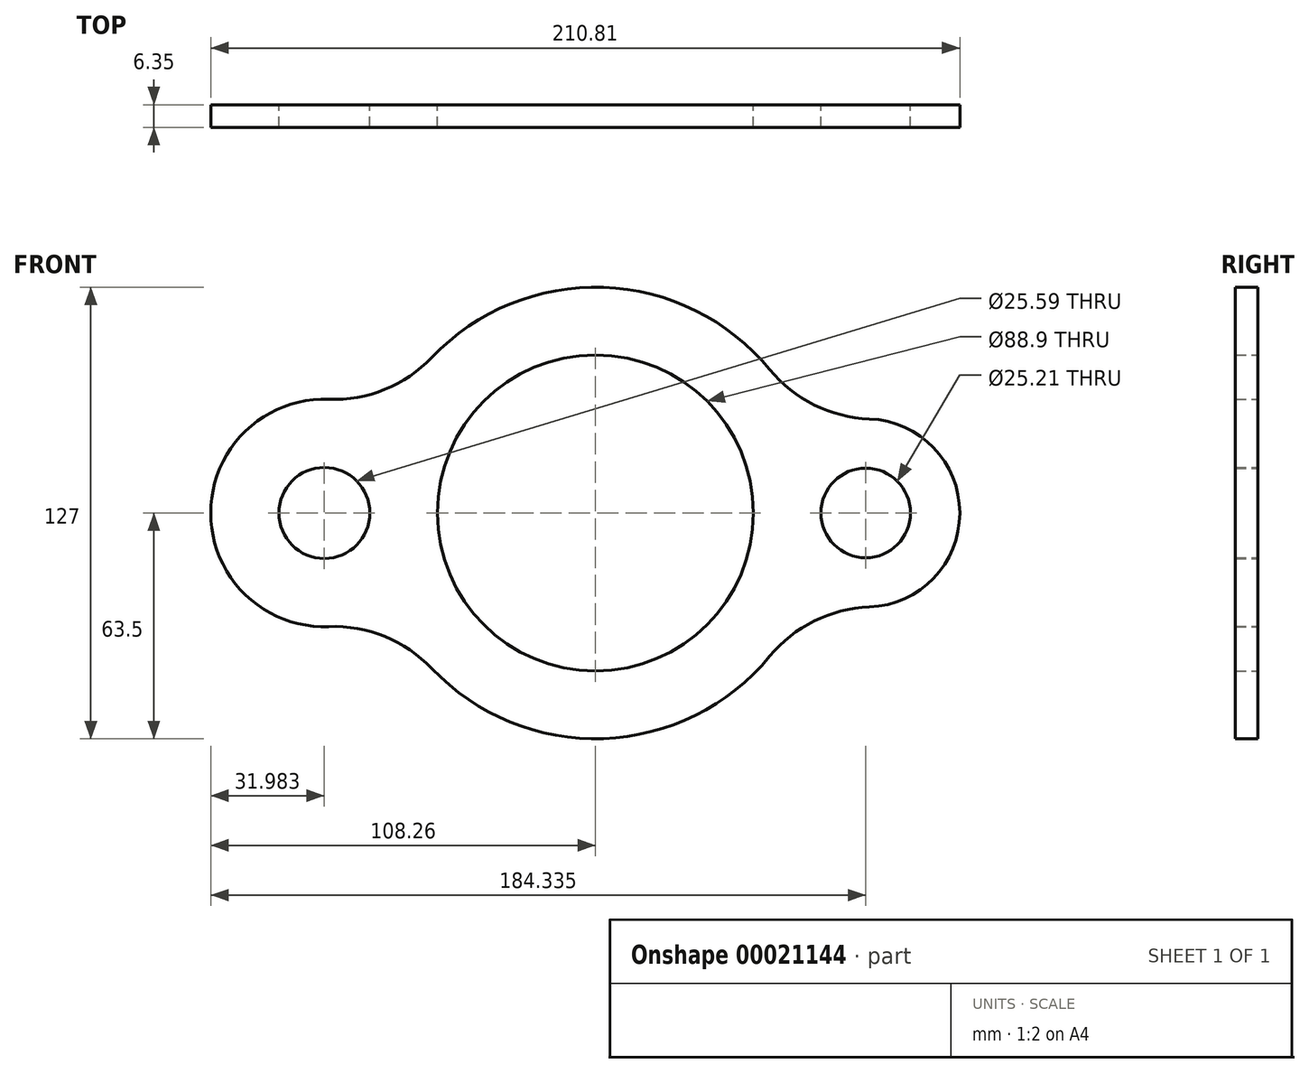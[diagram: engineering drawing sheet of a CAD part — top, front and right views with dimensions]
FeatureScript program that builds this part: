
annotation { "Feature Type Name" : "Feature", "Feature Type Description" : "" }
export const myFeature = defineFeature(function(context is Context, id is Id, definition is map)
    precondition{}
    {
        {
            var Q0;
            Q0=qCreatedBy(makeId("Front.planeOp"),FACE);
            var sketch = newSketch(context, id + "F0", { "sketchPlane" : qUnion([Q0])});
            skCircle(sketch, "E0", {"center": v(0, 0) * mm, "radius": 44.45 * mm});
            skPoint(sketch, "E1", {"position": v(-76.28, 0) * mm});
            skPoint(sketch, "E2", {"position": v(76.08, 0) * mm});
            skArc(sketch, "E3", {"start": v(-75.06, 31.96) * mm, "mid": v(-108.26, 0) * mm, "end": v(-75.06, -31.96) * mm});
            skCircle(sketch, "E4", {"center": v(-76.28, 0) * mm, "radius": 12.8 * mm});
            skCircle(sketch, "E5", {"center": v(76.08, 0) * mm, "radius": 12.6 * mm});
            skArc(sketch, "E6", {"start": v(77.06, -26.45) * mm, "mid": v(102.55, 0) * mm, "end": v(77.06, 26.45) * mm});
            skArc(sketch, "E7.trimOffspring", {"start": v(-46, -43.77) * mm, "mid": v(2.3, -63.46) * mm, "end": v(49.05, -40.33) * mm});
            skArc(sketch, "E8.trimOffspring", {"start": v(49.05, 40.33) * mm, "mid": v(2.3, 63.46) * mm, "end": v(-46, 43.77) * mm});
            skPoint(sketch, "E9.visualSharp", {"position": v(-57.86, 26.15) * mm});
            skArc(sketch, "E9.filletArc", {"start": v(-75.06, 31.96) * mm, "mid": v(-59.26, 34.74) * mm, "end": v(-46, 43.77) * mm});
            skPoint(sketch, "E10.visualSharp", {"position": v(59.93, 20.98) * mm});
            skArc(sketch, "E10.filletArc", {"start": v(49.05, 40.33) * mm, "mid": v(61.57, 30.39) * mm, "end": v(77.06, 26.45) * mm});
            skPoint(sketch, "E11.visualSharp", {"position": v(59.93, -20.98) * mm});
            skArc(sketch, "E11.filletArc", {"start": v(77.06, -26.45) * mm, "mid": v(61.57, -30.39) * mm, "end": v(49.05, -40.33) * mm});
            skPoint(sketch, "E12.visualSharp", {"position": v(-57.86, -26.15) * mm});
            skArc(sketch, "E12.filletArc", {"start": v(-46, -43.77) * mm, "mid": v(-59.26, -34.74) * mm, "end": v(-75.06, -31.96) * mm});
            skSolve(sketch);
        }
        {
            var Q0;
            Q0 = qSketchRegion(id + "F0", true);
            extrude(context, id + "F1", {"entities" : qUnion([Q0]), "depth" : 6.35 * mm});
        }
    });
